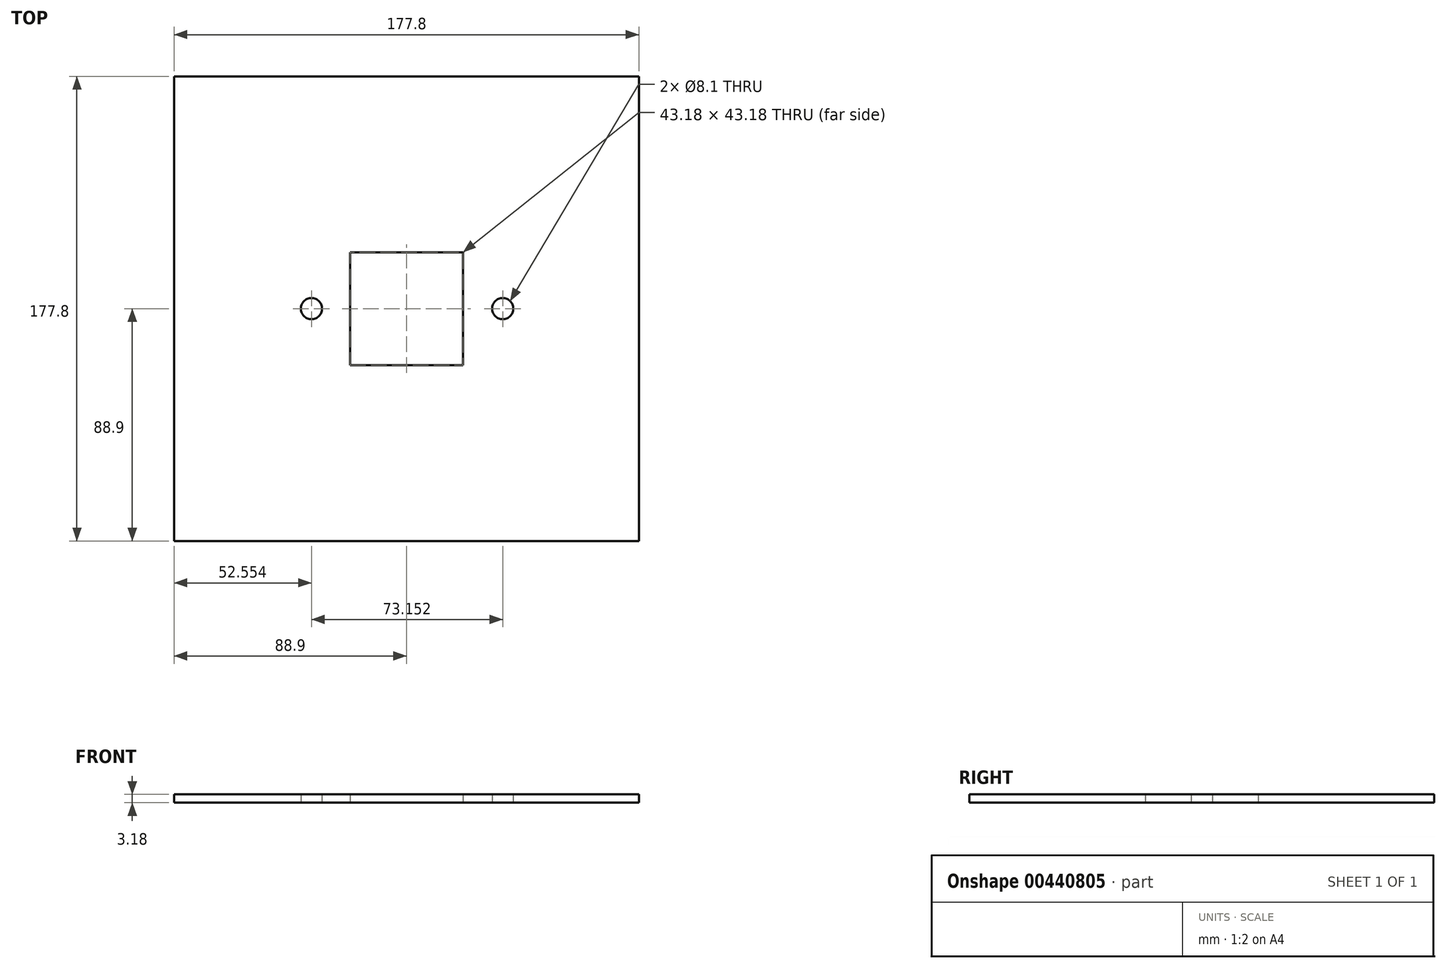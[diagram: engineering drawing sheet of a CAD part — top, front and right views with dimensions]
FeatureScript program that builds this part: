
annotation { "Feature Type Name" : "Feature", "Feature Type Description" : "" }
export const myFeature = defineFeature(function(context is Context, id is Id, definition is map)
    precondition{}
    {
        {
            var Q0;
            Q0=qCreatedBy(makeId("Top.planeOp"),FACE);
            var sketch = newSketch(context, id + "F0", { "sketchPlane" : qUnion([Q0])});
            skCircle(sketch, "E0", {"center": v(-36.35, 0) * mm, "radius": 4.05 * mm});
            skCircle(sketch, "E1", {"center": v(36.8, 0) * mm, "radius": 4.05 * mm});
            skLineSegment(sketch, "E2.bottom", {"start": v(88.9, 88.9) * mm, "end": v(-88.9, 88.9) * mm});
            skLineSegment(sketch, "E2.top", {"start": v(88.9, -88.9) * mm, "end": v(-88.9, -88.9) * mm});
            skLineSegment(sketch, "E2.left", {"start": v(88.9, 88.9) * mm, "end": v(88.9, -88.9) * mm});
            skLineSegment(sketch, "E2.right", {"start": v(-88.9, 88.9) * mm, "end": v(-88.9, -88.9) * mm});
            skLineSegment(sketch, "E3.bottom", {"start": v(21.59, 21.6) * mm, "end": v(-21.6, 21.6) * mm});
            skLineSegment(sketch, "E3.top", {"start": v(21.6, -21.6) * mm, "end": v(-21.59, -21.6) * mm});
            skLineSegment(sketch, "E3.left", {"start": v(21.59, 21.6) * mm, "end": v(21.6, -21.6) * mm});
            skLineSegment(sketch, "E3.right", {"start": v(-21.6, 21.6) * mm, "end": v(-21.59, -21.6) * mm});
            skPoint(sketch, "E3.middle", {"position": v(0, 0) * mm});
            skSolve(sketch);
        }
        {
            var Q0;
            Q0=qSketchRegion(id+"F0",true);
            extrude(context, id + "F1", {"entities" : qUnion([Q0]), "depth" : 3.17 * mm});
        }
    });
